# Revit family: 48102131(2021)
name_source: partatom
category: Plumbing Fixtures
revit_build: Autodesk Revit 2018 (Build: 20170223_1515(x64)
units: mm (PartAtom-declared; Revit-internal decimal feet)

## family parameters
Always vertical = Yes
Cut with Voids When Loaded = No
OmniClass Number = 23.45.55.00
OmniClass Title = Sanitary Faucets, Wastes
Part Type = Normal
Room Calculation Point = No
Round Connector Dimension = Use Diameter
Shared = No
Work Plane-Based = No

## types (1)
- 48102131 Bath and shower faucet with shower set
    2D/3D/BIM Files URL = http://static.hansa.com
    3D View = https://static.hansa.com
    Additional Features = protected against back-flow in domestic use (according to DIN EN 1717)
    Advanced Features = Inner body made of DZR brass;Thermal disinfection without cartridge readjustment;Flexible length / can be shortened
    Aerator = Standard aerator
    AssetType = Fixed
    BIMObjectName = 48102131(2021)
    Backflow Prevention EN1717 = EB
    BodyMaterial = Brass
    Brand = HANSA
    Catalog Drawing URL = http://static.hansa.com
    Category = Bathroom
    CloseOffRating = 0
    Color = Chrome
    Connection = Eccentric coupling(s);Cover plate(s);Silencer(s)
    Dimension Drawing URL = http://static.hansa.com
    Diverter = Turn operated diverter;Integrated into flow control handle
    DurationUnit = Year
    EAN Number = 4015474259355
    EN Standard = EN 1111, EN 1112, EN 1113
    ETIM Class Number = EC010862 Bath mixing tap
    FDV Document URL = http://www.hansa.com
    FaucetMainMaterial = Brass
    FaucetNominalDepth = 203 mm
    FaucetNominalHeight = 66 mm
    FaucetNominalWidth = 281 mm
    Features = Thermostatic
    Finish = Polished
    Flow Drawing URL = http://static.hansa.com
    Flow Rate At 300kPa = 360.3 L/s
    FlowCoefficient = 0
    Group = Bath and shower faucet
    Hand Shower Size = Ø 95 mm
    HandShowerNominalDepth = 185 mm
    HandShowerNominalHeight = 952 mm
    HandShowerNominalWidth = 145 mm
    IfcExportAs = IfcValveType
    IfcExportType = FAUCET
    Installation Type = Wall mounted
    Installation Width = cc150 ± 15 mm
    Installation and Maintenance Guide URL = http://static.hansa.com
    Interactive AR View URL = https://static.hansa.com
    Lever Handle = Temperature control handle;Flow control handle
    Manufacturer = HANSA
    ManufacturerName = HANSA
    ManufacturerURL = http://www.hansa.com
    Market = Austria;Belgium;Czech Republic;Germany;Spain;France;International;Italy;Netherlands;Slovakia
    Material = Brass
    Max. Hot Water Supply = 80 °C
    Mechanical Parts = Thermostatic cartridge for automatic temperature control;Litter filter(s);Non-return valve(s)
    Mobile Product Information URL = http://mpi.hansa.com
    Model = 48102131 Bath and shower faucet with shower set
    ModelReference = 48102131
    NBSDescription = Water supply fittings for baths
    NBSReference = 45-35-70/315
    Name = 48102131 Bath and shower faucet with shower set
    Name_en = 48102131 Bath and shower faucet with shower set
    Product Code = 48102131
    Product Family = HANSAPRISMA Eco
    Product Image URL = http://static.hansa.com
    Product URL = http://static.hansa.com
    Revision = 1
    Sales Package dimensions (LxWxH) = 959 x 203 x 108
    Shape = Sculptured
    Shower Parts = Soap dish;Shower hose (1750 mm);Eco flow control
    Shower Spray = Normal;Refreshing;Relaxing
    Shower Spray Number = 3 shower sprays
    Size = Faucet: 280x205x65 mm; Shower: 145x185x955 mm
    Spare-Part Information URL = http://static.hansa.com
    Surface treatment = Chrome
    Technical DataSheet URL = http://www.hansa.com
    Temperature = Thermostatic temperature control
    Temperature Adjustments = Adjustable hot water stop (included, retrofittable);Safety stop against scalding at 38°C
    UNSPSC Class Number = 30181700 Faucets or taps
    URL Declaration of Conformity = http://static.hansa.com
    URL REACH = http://static.hansa.com
    Uniclass2 = Pr_40_30_96_10
    Uniclass2015Description = Bath thermostatic water supply sets
    Uniclass2015Reference = Pr_40_20_87_10
    Version = 2
    VersionDate = 01/07/2022
    Warranty Information URL = http://warranty.hansa.com
    WarrantyDescription = http://warranty.hansa.com
    WarrantyDurationUnit = Year
    Working Pressure = 100 - 1000 kPa
    WorkingPressure = 100 - 1000 kPa

## geometry (parser evidence)
native form markers: Sweep x8
no freeform markers — native parametric forms only
